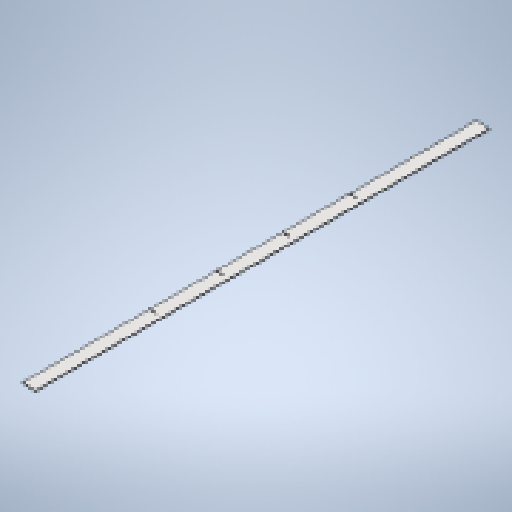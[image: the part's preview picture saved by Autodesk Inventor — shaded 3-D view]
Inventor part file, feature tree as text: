
AUTODESK INVENTOR PART (.ipt)
format: ipt  version: 2025 (Build 290162010, 162A)  size: 311,808 bytes
history: native  units: mm
features: other x3, sketch x3, sheet_metal_op x1, extrude x1, chamfer x1
ambient origin geometry x8: Origin, YZ Plane, XZ Plane, XY Plane, X Axis, Y Axis, Z Axis, Center Point
bodies: Solid1 (feature_tree)
feature tree (9):
  sheet_metal_op  "Face1"
  extrude  "Extrusion1"  Depth=1700.0mm
  chamfer  "Corner Round3"
  other  "Mark1"
  sketch  "Sketch1"  dims[d0=50.0mm d1=1700.0mm]
  other  "Plate1"
  sketch  "Sketch2"  dims[d2=3.0mm]
  sketch  "Sketch3"  dims[d15=26.0mm d16=3.0mm d17=170.0mm d18=0.0mm d19=0.0mm d20=26.0mm d21=3.0mm d22=340.0mm d23=26.0mm d24=3.0mm d25=170.0mm d26=340.0mm d27=3.0mm d28=26.0mm d29=6.0mm]
  other  "Definition1"
